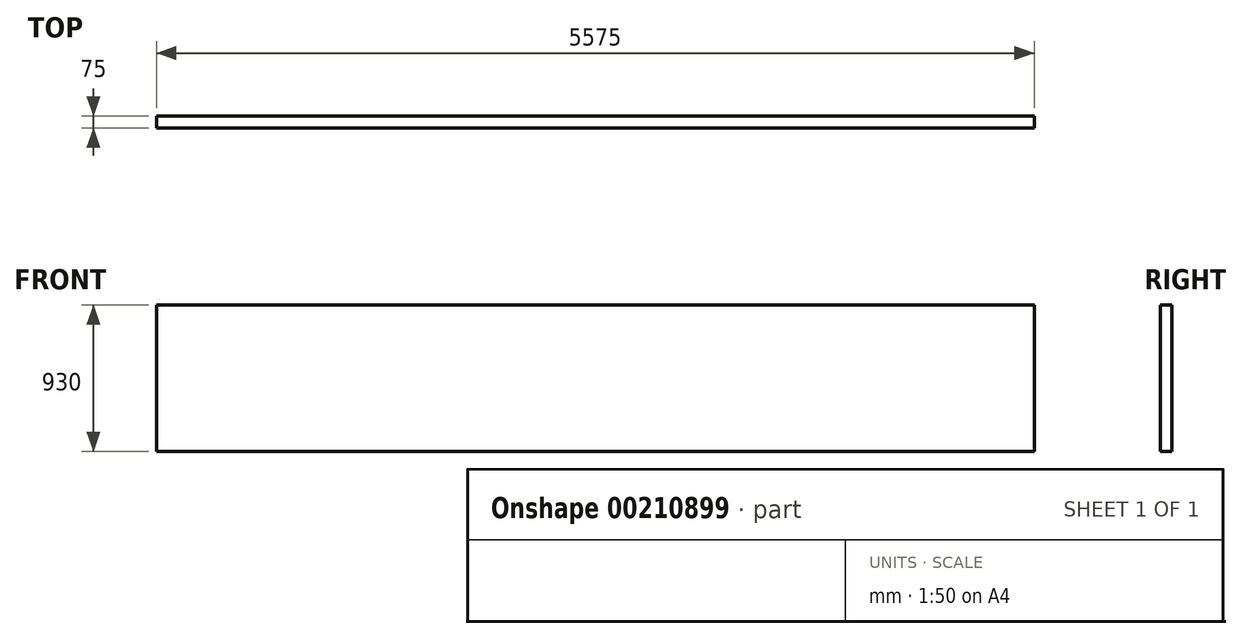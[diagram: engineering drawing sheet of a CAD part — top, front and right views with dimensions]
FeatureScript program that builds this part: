
annotation { "Feature Type Name" : "Feature", "Feature Type Description" : "" }
export const myFeature = defineFeature(function(context is Context, id is Id, definition is map)
    precondition{}
    {
        {
            var Q0;
            Q0=qCreatedBy(makeId("Front.planeOp"),FACE);
            var sketch = newSketch(context, id + "F0", { "sketchPlane" : qUnion([Q0])});
            skLineSegment(sketch, "E0.bottom", {"start": v(0, 0) * mm, "end": v(5575, 0) * mm});
            skLineSegment(sketch, "E0.top", {"start": v(0, 930) * mm, "end": v(5575, 930) * mm});
            skLineSegment(sketch, "E0.left", {"start": v(0, 0) * mm, "end": v(0, 930) * mm});
            skLineSegment(sketch, "E0.right", {"start": v(5575, 0) * mm, "end": v(5575, 930) * mm});
            skSolve(sketch);
        }
        {
            var Q0;
            Q0=makeQuery(id+"F0.imprint","IMPRINT",FACE,{"disambiguationData":[TD([[makeQuery(id+"F0.imprint","IMPRINT",EDGE,{"derivedFrom":sQuery(id+"F0.wireOp",EDGE,"E0.bottom")}),1.0]])]});
            extrude(context, id + "F1", {"entities" : qUnion([Q0]), "depth" : 75 * mm});
        }
    });
